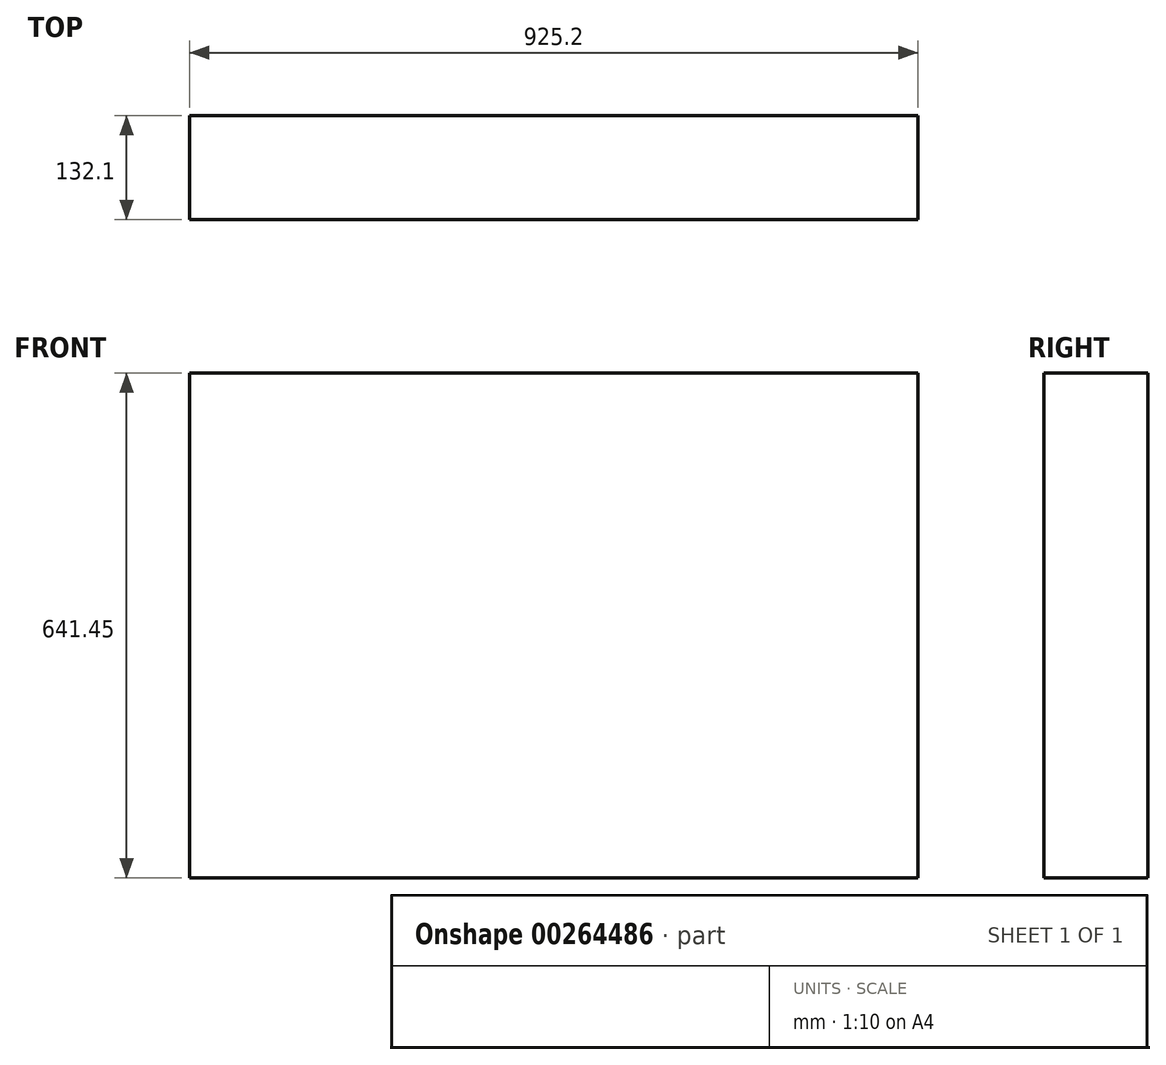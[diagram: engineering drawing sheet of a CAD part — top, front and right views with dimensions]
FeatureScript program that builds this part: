
annotation { "Feature Type Name" : "Feature", "Feature Type Description" : "" }
export const myFeature = defineFeature(function(context is Context, id is Id, definition is map)
    precondition{}
    {
        {
            var Q0;
            Q0=qCreatedBy(makeId("Top.planeOp"),FACE);
            var sketch = newSketch(context, id + "F0", { "sketchPlane" : qUnion([Q0])});
            skLineSegment(sketch, "E0.bottom", {"start": v(-462.6, 132.1) * mm, "end": v(462.6, 132.1) * mm});
            skLineSegment(sketch, "E0.top", {"start": v(-462.6, 0) * mm, "end": v(462.6, 0) * mm});
            skLineSegment(sketch, "E0.left", {"start": v(-462.6, 132.1) * mm, "end": v(-462.6, 0) * mm});
            skLineSegment(sketch, "E0.right", {"start": v(462.6, 132.1) * mm, "end": v(462.6, 0) * mm});
            skSolve(sketch);
        }
        {
            var Q0;
            Q0 = qSketchRegion(id + "F0", true);
            extrude(context, id + "F1", {"entities" : qUnion([Q0]), "depth" : 641.45 * mm});
        }
    });
